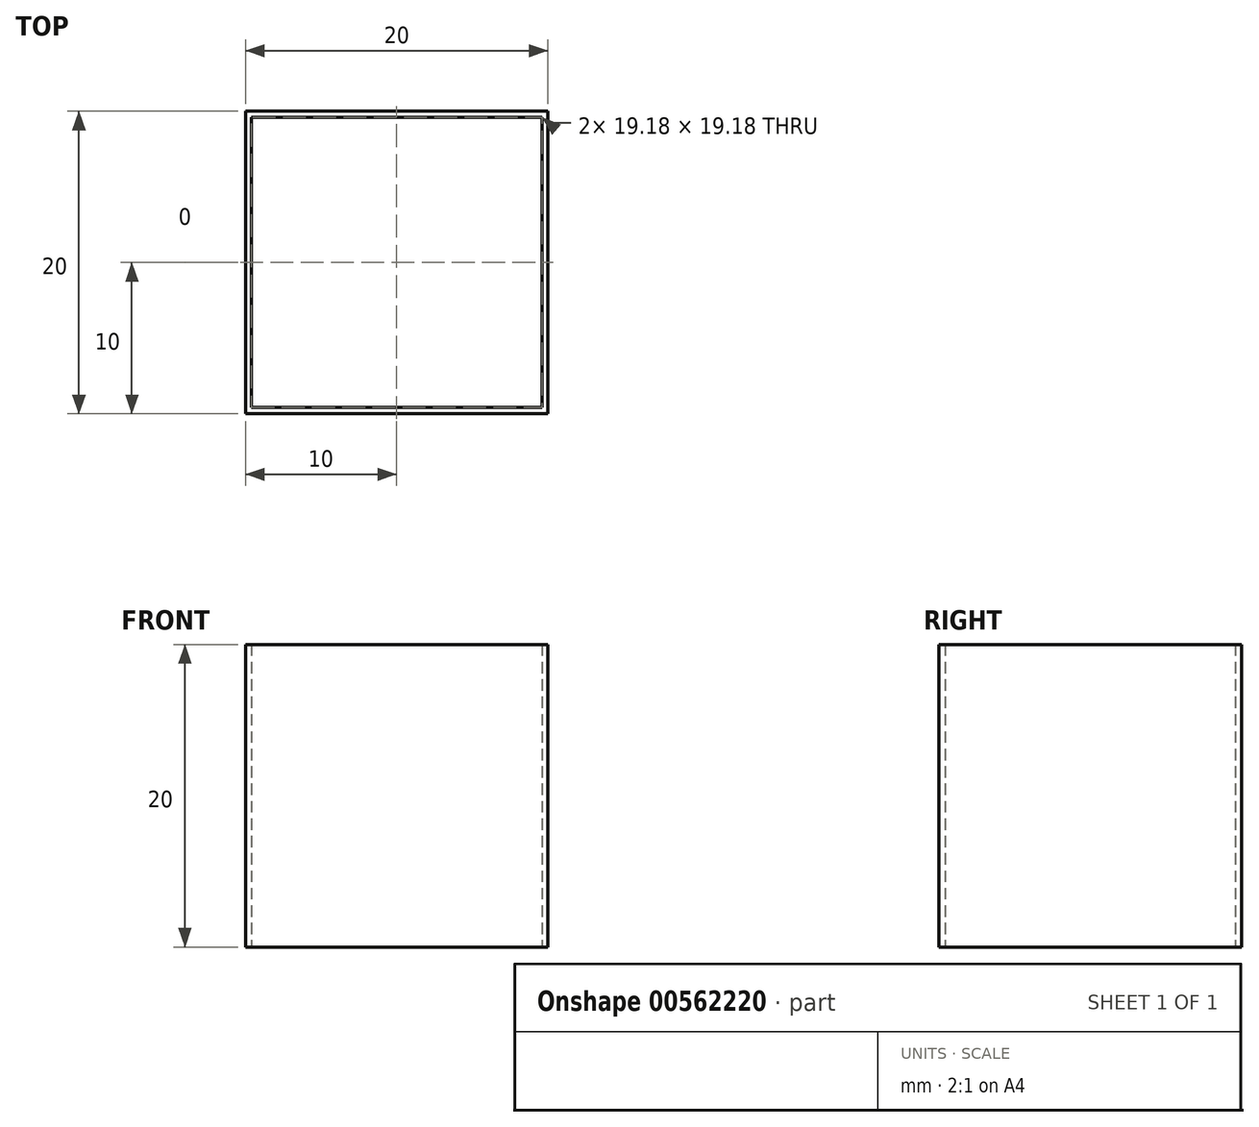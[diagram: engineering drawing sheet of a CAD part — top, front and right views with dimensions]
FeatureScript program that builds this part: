
annotation { "Feature Type Name" : "Feature", "Feature Type Description" : "" }
export const myFeature = defineFeature(function(context is Context, id is Id, definition is map)
    precondition{}
    {
        {
            var Q0;
            Q0=qCreatedBy(makeId("Top.planeOp"),FACE);
            var sketch = newSketch(context, id + "F0", { "sketchPlane" : qUnion([Q0])});
            skLineSegment(sketch, "E0.bottom", {"start": v(10, -10) * mm, "end": v(-10, -10) * mm});
            skLineSegment(sketch, "E0.top", {"start": v(10, 10) * mm, "end": v(-10, 10) * mm});
            skLineSegment(sketch, "E0.left", {"start": v(10, -10) * mm, "end": v(10, 10) * mm});
            skLineSegment(sketch, "E0.right", {"start": v(-10, -10) * mm, "end": v(-10, 10) * mm});
            skPoint(sketch, "E0.middle", {"position": v(0, 0) * mm});
            skSolve(sketch);
        }
        {
            var Q0;
            Q0 = qSketchRegion(id + "F0", true);
            extrude(context, id + "F1", {"entities" : qUnion([Q0]), "depth" : 20 * mm, "offsetDistance" : 25 * mm});
        }
        {
            var Q0;
            Q0=makeQuery(id+"F1.opExtrude","CAP_FACE",FACE,{"disambiguationData":[OSD([sQuery(id+"F0.wireOp",EDGE,"E0.bottom"),sQuery(id+"F0.wireOp",EDGE,"E0.top"),sQuery(id+"F0.wireOp",EDGE,"E0.left"),sQuery(id+"F0.wireOp",EDGE,"E0.right")])],"isStart":false});
            var Q1;
            Q1=makeQuery(id+"F1.opExtrude","CAP_FACE",FACE,{"disambiguationData":[OSD([sQuery(id+"F0.wireOp",EDGE,"E0.bottom"),sQuery(id+"F0.wireOp",EDGE,"E0.top"),sQuery(id+"F0.wireOp",EDGE,"E0.left"),sQuery(id+"F0.wireOp",EDGE,"E0.right")])],"isStart":true});
            shell(context, id + "F2", {"entities" : qUnion([Q0, Q1]), "thickness" : .41 * mm});
        }
    });
